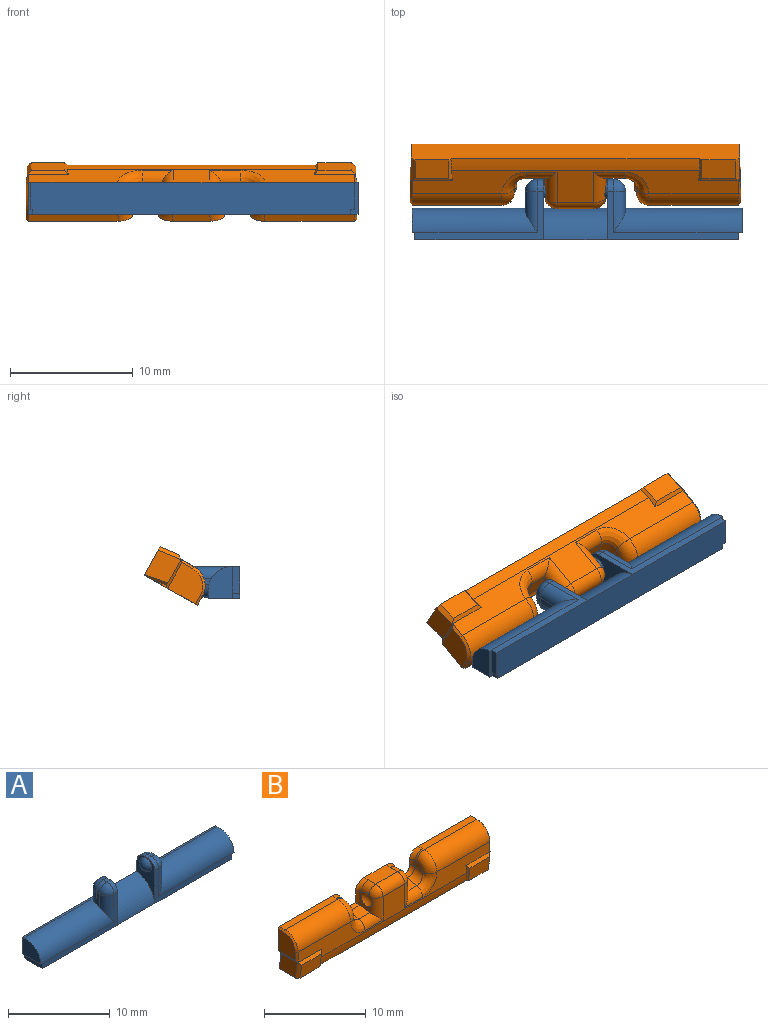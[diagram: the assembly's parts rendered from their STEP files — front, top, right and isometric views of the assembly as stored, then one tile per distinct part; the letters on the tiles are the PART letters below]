
ASSEMBLY  parts=2 mates=1
PART A: 41 faces, bbox 26.9x2.6x5 mm
  f0: plane 0.6x0.4mm, normal (1,0,0), area 0.2mm2, adj f9,f11,f15,f40
  f1: plane 0.6x0.4mm, normal (-1,0,0), area 0.2mm2, adj f7,f12,f15,f40
  f2: plane 10.7x3.95mm, normal (0,-1,0), area 8.1mm2, adj f4,f10,f30,f31,f38,f40
  f3: plane 10.5x3.95mm, normal (0,-1,0), area 8mm2, adj f5,f8,f23,f24,f39,f40
  f4: plane 4.95x2.5mm, normal (-1,0,0), area 5.4mm2, adj f2,f6,f17,f18,f31,f34,f37,f40
  f5: plane 4.95x2.5mm, normal (1,0,0), area 5.8mm2, adj f3,f6,f19,f21,f22,f23,f26,f40
  f6: cylinder r=3mm len=26.9mm, axis (-1,0,0), area 25.1mm2, adj f4,f5,f13,f14,f15,f17,f19,f29
  f7: plane 0.6x0.1mm, normal (0,1,0), area 0.1mm2, adj f1,f8,f12,f40
  f8: plane 2.2x0.6mm, normal (-1,0,0), area 1.3mm2, adj f3,f7,f12,f40
  f9: plane 0.6x0.3mm, normal (0,1,0), area 0.2mm2, adj f0,f10,f11,f40
  f10: plane 2.2x0.6mm, normal (1,0,0), area 1.3mm2, adj f2,f9,f11,f40
  f11: plane 2.6x0.6mm, normal (0,0,-1), area 0.9mm2, adj f0,f9,f10,f14,f15,f38
  f12: plane 2.6x0.3mm, normal (0,0,-1), area 0.6mm2, adj f1,f7,f8,f13,f15,f39
  f13: plane 2.6x2mm, normal (-1,0,0), area 4.3mm2, adj f6,f12,f15,f39
  f14: plane 2.6x2mm, normal (1,0,0), area 4.3mm2, adj f6,f11,f15,f38
  f15: plane 26.9x2.6mm, normal (0,1,0), area 69.4mm2, adj f0,f1,f6,f11,f12,f13,f14,f40
  f16: plane 1.62x0.5mm, normal (1,0,0), area 0.8mm2, adj f30,f33,f36,f38
  f17: plane 1.37x0.5mm, normal (0,1,0), area 0.7mm2, adj f4,f6,f34,f36
  f18: plane 0.5x0.5mm, normal (0,0,1), area 0.3mm2, adj f4,f31,f33,f34
  f19: plane 1.37x0.5mm, normal (0,1,0), area 0.7mm2, adj f5,f6,f26,f29
  f20: plane 1.62x0.5mm, normal (-1,0,0), area 0.8mm2, adj f24,f27,f29,f39
  f21: plane 0.5x0.5mm, normal (0,0,1), area 0.2mm2, adj f5,f23,f26,f27
  f22: sphere r=0.81mm, area 2mm2, adj f5
  f23: cylinder r=1mm len=1mm, axis (-1,0,0), area 0.8mm2, adj f3,f5,f21,f25
  f24: cylinder r=1mm len=3.35mm, axis (0,0,1), area 3.7mm2, adj f3,f20,f25,f39
  f25: sphere r=1mm, area 1.6mm2, adj f23,f24,f27
  f26: cylinder r=1mm len=1mm, axis (1,0,0), area 0.8mm2, adj f5,f19,f21,f28
  f27: cylinder r=1mm len=1mm, axis (0,1,0), area 0.8mm2, adj f20,f21,f25,f28
  f28: sphere r=1mm, area 1.6mm2, adj f26,f27,f29
  f29: cylinder r=1mm len=1.41mm, axis (0,0,-1), area 2.2mm2, adj f6,f19,f20,f28,f39
  f30: cylinder r=1mm len=3.35mm, axis (0,0,-1), area 3.7mm2, adj f2,f16,f32,f38
  f31: cylinder r=1mm len=1mm, axis (-1,0,0), area 0.8mm2, adj f2,f4,f18,f32
  f32: sphere r=1mm, area 1.6mm2, adj f30,f31,f33
  f33: cylinder r=1mm len=1mm, axis (0,-1,0), area 0.8mm2, adj f16,f18,f32,f35
  f34: cylinder r=1mm len=1mm, axis (1,0,0), area 0.8mm2, adj f4,f17,f18,f35
  f35: sphere r=1mm, area 1.6mm2, adj f33,f34,f36
  f36: cylinder r=1mm len=1.41mm, axis (0,0,1), area 2.2mm2, adj f6,f16,f17,f35,f38
  f37: sphere r=0.81mm, area 3mm2, adj f4
  f38: cylinder r=2mm len=10.5mm, axis (-1,0,0), area 34.4mm2, adj f2,f6,f11,f14,f16,f30,f36
  f39: cylinder r=2mm len=10.2mm, axis (-1,0,0), area 33.4mm2, adj f3,f6,f12,f13,f20,f24,f29
  f40: plane 26.4x2.6mm, normal (0,0,-1), area 68.4mm2, adj f0,f1,f2,f3,f4,f5,f6,f7
PART B: 78 faces, bbox 27.1x4.1x5.1 mm
  f0: plane 0.31x0.1mm, normal (0,0,-1), area 0mm2, adj f8,f13,f15,f17
  f1: cylinder r=9.35mm len=20.29mm, axis (1,0,0), area 20.5mm2, adj f35,f71,f75,f77
  f2: plane 2.6x0.27mm, normal (-0.71,0,-0.71), area 0.7mm2, adj f3,f9,f17,f35,f66,f70,f76
  f3: plane 0.31x0.1mm, normal (0,0,-1), area 0mm2, adj f2,f14,f16,f17
  f4: plane 7.39x0.8mm, normal (0,0,1), area 5.9mm2, adj f7,f17,f23,f42,f58
  f5: plane 7.39x0.8mm, normal (0,0,1), area 5.9mm2, adj f10,f17,f32,f54,f56
  f6: plane 2.6x2.4mm, normal (1,0,0), area 5.7mm2, adj f7,f8,f17,f63,f64
  f7: plane 0.8x0.2mm, normal (0.71,0,0.71), area 0.2mm2, adj f4,f6,f17,f63
  f8: plane 2.6x0.27mm, normal (0.71,0,-0.71), area 0.7mm2, adj f0,f6,f17,f35,f64,f68,f72
  f9: plane 2.6x2.4mm, normal (-1,0,0), area 5.7mm2, adj f2,f10,f17,f65,f66
  f10: plane 0.8x0.2mm, normal (-0.71,0,0.71), area 0.2mm2, adj f5,f9,f17,f65
  f11: plane 2.52x2mm, normal (1,0,0), area 4.4mm2, adj f13,f68,f72,f73,f77
  f12: plane 2.52x2mm, normal (-1,0,0), area 4.4mm2, adj f14,f70,f74,f76,f77
  f13: plane 2x0.41mm, normal (0.71,0.7,0.12), area 0.5mm2, adj f0,f11,f15,f17,f68,f77
  f14: plane 2x0.41mm, normal (-0.71,0.7,0.12), area 0.5mm2, adj f3,f12,f16,f17,f70,f77
  f15: plane 1.16x0.2mm, normal (1,0,0), area 0.1mm2, adj f0,f13,f17
  f16: plane 1.16x0.2mm, normal (-1,0,0), area 0.1mm2, adj f3,f14,f17
  f17: plane 27.07x5.07mm, normal (0,1,0), area 122.9mm2, adj f0,f2,f3,f4,f5,f6,f7,f8
  f18: plane 1x0.81mm, normal (-1,0,0), area 0.6mm2, adj f21,f42,f43,f44,f59
  f19: plane 1x0.81mm, normal (1,0,0), area 0.6mm2, adj f31,f51,f54,f55,f57
  f20: plane 3.18x1.6mm, normal (0,0,1), area 4.8mm2, adj f17,f26,f29,f47,f49,f61
  f21: cylinder r=1mm len=0.63mm, axis (0,0,-1), area 0.4mm2, adj f17,f18,f22,f23
  f22: sphere r=1mm, area 0.8mm2, adj f17,f21,f24,f43
  f23: torus R=2mm, axis (0,0,1), area 1mm2, adj f4,f17,f21,f42
  f24: cylinder r=1mm len=1.49mm, axis (-1,0,0), area 0.7mm2, adj f17,f22,f25,f37
  f25: cylinder r=1mm len=1.65mm, axis (0,0,1), area 1mm2, adj f17,f24,f26,f34,f36,f37,f41
  f26: torus R=2mm, axis (0,0,1), area 1mm2, adj f17,f20,f25,f47
  f27: cylinder r=1mm len=1.65mm, axis (0,0,1), area 1mm2, adj f17,f28,f29,f33,f38,f39,f40
  f28: cylinder r=1mm len=1.49mm, axis (-1,0,0), area 0.7mm2, adj f17,f27,f30,f39
  f29: torus R=2mm, axis (0,0,1), area 1mm2, adj f17,f20,f27,f49
  f30: sphere r=1mm, area 0.8mm2, adj f17,f28,f31,f51
  f31: cylinder r=1mm len=0.63mm, axis (0,0,-1), area 0.4mm2, adj f17,f19,f30,f32
  f32: torus R=2mm, axis (0,0,1), area 1mm2, adj f5,f17,f31,f54
  f33: plane 1.05x1mm, normal (-1,0,0), area 0.5mm2, adj f27,f39,f40,f50
  f34: plane 1.05x1mm, normal (1,0,0), area 0.5mm2, adj f25,f37,f41,f48
  f35: plane 26.6x3mm, normal (0,-1,0), area 38.3mm2, adj f1,f2,f8,f44,f45,f46,f48,f50
  f36: plane 0.24x0.14mm, normal (1,0,0), area 0mm2, adj f25,f41,f47
  f37: plane 1.52x1.35mm, normal (0,-0.17,0.98), area 2.1mm2, adj f24,f25,f34,f43,f46,f48
  f38: plane 0.24x0.14mm, normal (-1,0,0), area 0mm2, adj f27,f40,f49
  f39: plane 1.52x1.35mm, normal (0,-0.17,0.98), area 2.1mm2, adj f27,f28,f33,f50,f51,f52
  f40: sphere r=0.94mm, area 2.5mm2, adj f27,f33,f38,f49,f50,f62
  f41: sphere r=0.94mm, area 2.5mm2, adj f25,f34,f36,f47,f48,f60
  f42: cylinder r=1mm len=1mm, axis (0,-1,0), area 0.3mm2, adj f4,f18,f23,f59
  f43: cylinder r=1mm len=1.52mm, axis (0,0.98,0.17), area 1.9mm2, adj f18,f22,f37,f45
  f44: cylinder r=1mm len=1mm, axis (0,0,1), area 0mm2, adj f18,f35,f45,f59
  f45: bspline ~2.38x2.35mm, area 3.2mm2, adj f35,f43,f44,f46
  f46: cylinder r=1mm len=2.5mm, axis (-1,0,0), area 2.7mm2, adj f35,f37,f45,f48
  f47: cylinder r=1mm len=1mm, axis (0,1,0), area 1.4mm2, adj f20,f26,f36,f41,f60
  f48: cylinder r=1mm len=2.84mm, axis (0,0,-1), area 3mm2, adj f34,f35,f37,f41,f46,f60
  f49: cylinder r=1mm len=1mm, axis (0,-1,0), area 1.4mm2, adj f20,f29,f38,f40,f62
  f50: cylinder r=1mm len=2.84mm, axis (0,0,1), area 3mm2, adj f33,f35,f39,f40,f52,f62
  f51: cylinder r=1mm len=1.52mm, axis (0,-0.98,-0.17), area 1.9mm2, adj f19,f30,f39,f53
  f52: cylinder r=1mm len=2.5mm, axis (-1,0,0), area 2.7mm2, adj f35,f39,f50,f53
  f53: bspline ~2.38x2mm, area 3.2mm2, adj f35,f51,f52,f55
  f54: cylinder r=1mm len=1mm, axis (0,1,0), area 0.3mm2, adj f5,f19,f32,f57
  f55: cylinder r=1mm len=1mm, axis (0,0,-1), area 0mm2, adj f19,f35,f53,f57
  f56: cylinder r=1.8mm len=7.3mm, axis (-1,0,0), area 20.6mm2, adj f5,f35,f57,f65
  f57: torus R=0.8mm, axis (1,0,0), area 3.5mm2, adj f19,f54,f55,f56
  f58: cylinder r=1.8mm len=7.3mm, axis (-1,0,0), area 20.6mm2, adj f4,f35,f59,f63
  f59: torus R=0.8mm, axis (1,0,0), area 3.5mm2, adj f18,f42,f44,f58
  f60: sphere r=1mm, area 1.5mm2, adj f41,f47,f48,f61
  f61: cylinder r=1mm len=3mm, axis (-1,0,0), area 4.7mm2, adj f20,f35,f60,f62
  f62: sphere r=1mm, area 1.5mm2, adj f40,f49,f50,f61
  f63: cone r=1.6mm half-angle=45deg, axis (-1,0,0), area 0.8mm2, adj f6,f7,f58,f64
  f64: plane 1.2x0.2mm, normal (0.71,-0.71,0), area 0.3mm2, adj f6,f8,f35,f63
  f65: cone r=1.6mm half-angle=45deg, axis (1,0,0), area 0.8mm2, adj f9,f10,f56,f66
  f66: plane 1.2x0.2mm, normal (-0.71,-0.71,0), area 0.3mm2, adj f2,f9,f35,f65
  f67: plane 2.76x1.64mm, normal (0,-0.99,-0.12), area 4.6mm2, adj f71,f72,f73,f77
  f68: plane 2.23x0.1mm, normal (0,0,1), area 0.2mm2, adj f8,f11,f13,f72
  f69: plane 2.76x1.64mm, normal (0,-0.99,-0.12), area 4.6mm2, adj f74,f75,f76,f77
  f70: plane 2.23x0.1mm, normal (0,0,1), area 0.2mm2, adj f2,f12,f14,f76
  f71: plane 1.96x0.45mm, normal (-0.71,-0.7,-0.09), area 0.5mm2, adj f1,f35,f67,f72,f77
  f72: plane 3.37x0.36mm, normal (0,-0.75,0.66), area 1.2mm2, adj f8,f11,f35,f67,f68,f71,f73
  f73: plane 1.96x0.52mm, normal (0.71,-0.7,-0.09), area 0.8mm2, adj f11,f67,f72,f77
  f74: plane 1.96x0.52mm, normal (-0.71,-0.7,-0.09), area 0.8mm2, adj f12,f69,f76,f77
  f75: plane 1.96x0.45mm, normal (0.71,-0.7,-0.09), area 0.5mm2, adj f1,f35,f69,f76,f77
  f76: plane 3.37x0.36mm, normal (0,-0.75,0.66), area 1.2mm2, adj f2,f12,f35,f69,f70,f74,f75
  f77: plane 26.8x2.65mm, normal (0,0,-1), area 66.6mm2, adj f1,f11,f12,f13,f14,f17,f67,f69
PLACE A rot(axis=(-1,0,0),90deg) t=(20.26,47,70.97)mm fixed
PLACE B rot(axis=(0,0.86,-0.51),180deg) t=(114.07,58.83,136.33)mm
MATE cylindrical A.f5 <-> B.f33  axis (1,0,0) through (27.06,52.5,40.2)mm
